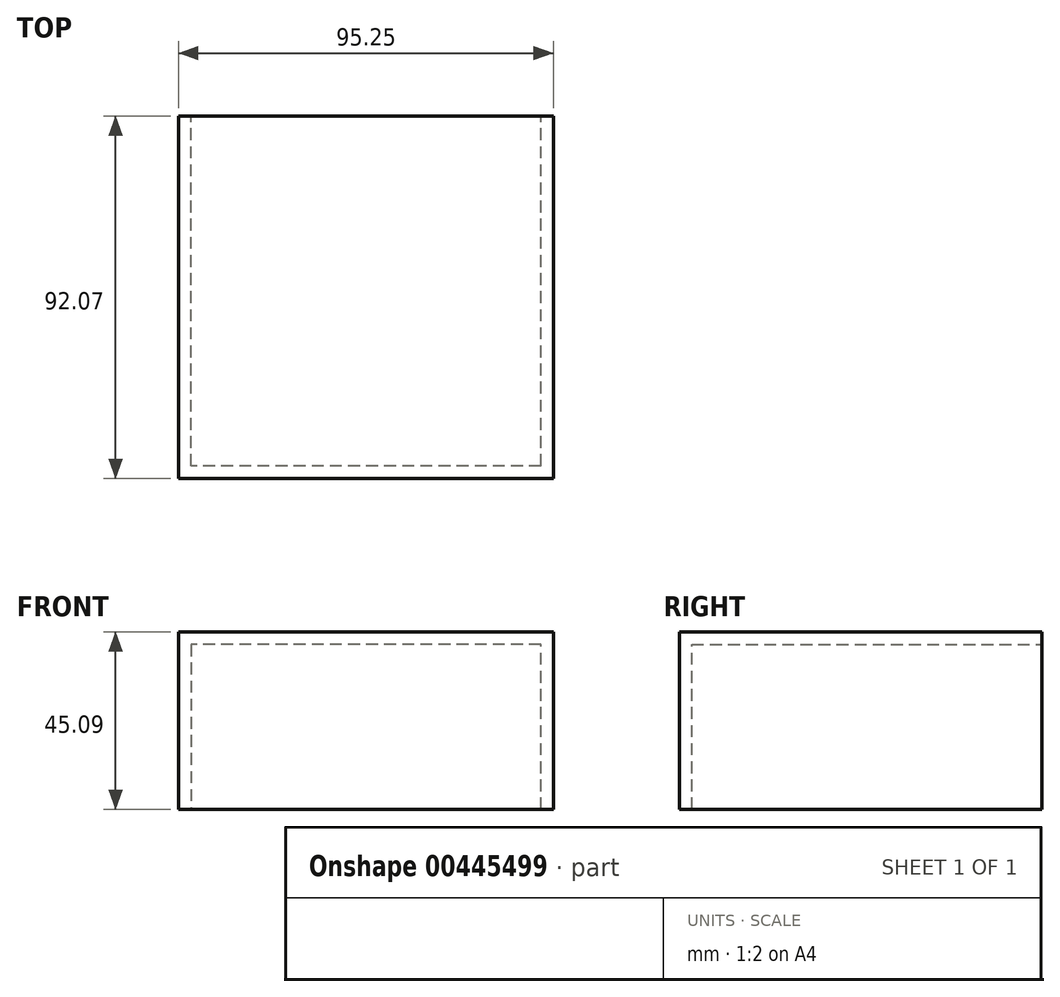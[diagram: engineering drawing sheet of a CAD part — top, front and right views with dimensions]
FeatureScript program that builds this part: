
annotation { "Feature Type Name" : "Feature", "Feature Type Description" : "" }
export const myFeature = defineFeature(function(context is Context, id is Id, definition is map)
    precondition{}
    {
        {
            var Q0;
            Q0=qCreatedBy(makeId("Front.planeOp"),FACE);
            var sketch = newSketch(context, id + "F0", { "sketchPlane" : qUnion([Q0])});
            skLineSegment(sketch, "E0", {"start": v(-34.9, -17.26) * mm, "end": v(-34.9, 24.65) * mm});
            skLineSegment(sketch, "E1", {"start": v(-34.9, 24.65) * mm, "end": v(54, 24.65) * mm});
            skLineSegment(sketch, "E2", {"start": v(54, 24.65) * mm, "end": v(54, -17.26) * mm});
            skLineSegment(sketch, "E3", {"start": v(-34.9, -17.26) * mm, "end": v(-38.07, -17.26) * mm});
            skLineSegment(sketch, "E4", {"start": v(-38.07, -17.26) * mm, "end": v(-38.07, 27.83) * mm});
            skLineSegment(sketch, "E5", {"start": v(-38.07, 27.83) * mm, "end": v(57.18, 27.83) * mm});
            skLineSegment(sketch, "E6", {"start": v(57.18, 27.83) * mm, "end": v(57.18, -17.26) * mm});
            skLineSegment(sketch, "E7", {"start": v(57.18, -17.26) * mm, "end": v(54, -17.26) * mm});
            skLineSegment(sketch, "E8.top", {"start": v(-38.07, -17.26) * mm, "end": v(57.18, -17.26) * mm});
            skLineSegment(sketch, "E8.left", {"start": v(-38.07, 27.83) * mm, "end": v(-38.07, -17.26) * mm});
            skArc(sketch, "E9", {"start": v(-5.18, 9.67) * mm, "mid": v(-18.9, 21.6) * mm, "end": v(-32.6, 9.67) * mm});
            skLineSegment(sketch, "E10", {"start": v(-32.6, 9.67) * mm, "end": v(-32.6, -17.26) * mm});
            skLineSegment(sketch, "E11", {"start": v(-5.18, 9.67) * mm, "end": v(-5.18, -17.26) * mm});
            skSolve(sketch);
        }
        {
            var Q0;
            {var subQ1=sQuery(id+"F0.wireOp",EDGE,"E0");Q0=makeQuery(id+"F0.imprint","IMPRINT",FACE,{"disambiguationData":[TD([[makeQuery(id+"F0.imprint","IMPRINT",EDGE,{"derivedFrom":subQ1}),1.0]])]});}
            extrude(context, id + "F1", {"entities" : qUnion([Q0]), "depth" : 114.3 * mm});
        }
        {
            var Q0;
            Q0=qCreatedBy(makeId("Front.planeOp"),FACE);
            var sketch = newSketch(context, id + "F2", { "sketchPlane" : qUnion([Q0])});
            skLineSegment(sketch, "E12.bottom", {"start": v(-38.05, 27.67) * mm, "end": v(57.2, 27.67) * mm});
            skLineSegment(sketch, "E12.top", {"start": v(-38.05, -17.41) * mm, "end": v(57.2, -17.41) * mm});
            skLineSegment(sketch, "E12.left", {"start": v(-38.05, 27.67) * mm, "end": v(-38.05, -17.41) * mm});
            skLineSegment(sketch, "E12.right", {"start": v(57.2, 27.67) * mm, "end": v(57.2, -17.41) * mm});
            skSolve(sketch);
        }
        {
            var Q0;
            Q0=makeQuery(id+"F1.opExtrude","CAP_FACE",FACE,{"disambiguationData":[OSD([sQuery(id+"F0.wireOp",EDGE,"E0"),sQuery(id+"F0.wireOp",EDGE,"E1"),sQuery(id+"F0.wireOp",EDGE,"E2"),sQuery(id+"F0.wireOp",EDGE,"E5"),sQuery(id+"F0.wireOp",EDGE,"E8.top"),sQuery(id+"F0.wireOp",EDGE,"E8.left"),sQuery(id+"F0.wireOp",EDGE,"E6")])],"isStart":false});
            var sketch = newSketch(context, id + "F3", { "sketchPlane" : qUnion([Q0])});
            skLineSegment(sketch, "E13.bottom", {"start": v(-38.07, 27.83) * mm, "end": v(57.18, 27.83) * mm});
            skLineSegment(sketch, "E13.top", {"start": v(-38.07, -17.26) * mm, "end": v(57.18, -17.26) * mm});
            skLineSegment(sketch, "E13.left", {"start": v(-38.07, 27.83) * mm, "end": v(-38.07, -17.26) * mm});
            skLineSegment(sketch, "E13.right", {"start": v(57.18, 27.83) * mm, "end": v(57.18, -17.26) * mm});
            skSolve(sketch);
        }
        {
            var Q0;
            Q0 = qSketchRegion(id + "F3", true);
            var Q1;
            Q1 = qSketchRegion(id + "F0", true);
            extrude(context, id + "F4", {"entities" : qUnion([Q0, Q1]), "operationType" : NewBodyOperationType.ADD, "depth" : 3.17 * mm});
        }
        {
            var Q0;
            Q0=makeQuery(id+"F2.imprint","IMPRINT",FACE,{"disambiguationData":[TD([[makeQuery(id+"F2.imprint","IMPRINT",EDGE,{"derivedFrom":sQuery(id+"F2.wireOp",EDGE,"E12.bottom")}),-1.0]])]});
            var sketch = newSketch(context, id + "F5", { "sketchPlane" : qUnion([Q0])});
            skCircle(sketch, "E14", {"center": v(-21.16, 10.78) * mm, "radius": 13.72 * mm});
            skLineSegment(sketch, "E15.bottom", {"start": v(-7.44, 10.78) * mm, "end": v(-34.88, 10.78) * mm});
            skLineSegment(sketch, "E15.top", {"start": v(-7.44, -18.14) * mm, "end": v(-34.88, -18.14) * mm});
            skLineSegment(sketch, "E15.left", {"start": v(-7.44, 10.78) * mm, "end": v(-7.44, -18.14) * mm});
            skLineSegment(sketch, "E15.right", {"start": v(-34.88, 10.78) * mm, "end": v(-34.88, -18.14) * mm});
            skSolve(sketch);
        }
        {
            var Q0;
            Q0=sQuery(id+"F5.wireOp",VERTEX,"E14.center");
            var Q1;
            Q1=makeQuery(id+"F1.opExtrude","SWEPT_BODY",BODY,{"disambiguationData":[OSD([sQuery(id+"F0.wireOp",EDGE,"E0"),sQuery(id+"F0.wireOp",EDGE,"E1"),sQuery(id+"F0.wireOp",EDGE,"E2"),sQuery(id+"F0.wireOp",EDGE,"E5"),sQuery(id+"F0.wireOp",EDGE,"E8.top"),sQuery(id+"F0.wireOp",EDGE,"E8.left"),sQuery(id+"F0.wireOp",EDGE,"E6")])]});
            hole(context, id + "F6", {"style" : HoleStyle.SIMPLE, "endStyle" : HoleEndStyle.BLIND, "oppositeDirection" : true, "holeDiameter" : 27.43 * mm, "holeDepth" : 3.17 * mm, "tappedDepth" : 12.7 * mm, "tapClearance" : 3, "startFromSketch" : true, "locations" : qUnion([Q0]), "scope" : qUnion([Q1])});
        }
        {
            var Q0;
            Q0 = qSketchRegion(id + "F5", true);
            extrude(context, id + "F7", {"entities" : qUnion([Q0]), "operationType" : NewBodyOperationType.REMOVE, "depth" : 3.17 * mm});
        }
        {
            var Q0;
            Q0=makeQuery(id+"F4.boolean.opBoolean","MERGE",FACE,{"derivedFrom":[makeQuery(id+"F1.opExtrude","SWEPT_FACE",FACE,{"disambiguationData":[OSD([sQuery(id+"F0.wireOp",EDGE,"E5")])]}),makeQuery(id+"F4.opExtrude","SWEPT_FACE",FACE,{"disambiguationData":[OSD([sQuery(id+"F3.wireOp",EDGE,"E13.bottom")])]})]});
            var sketch = newSketch(context, id + "F8", { "sketchPlane" : qUnion([Q0])});
            skLineSegment(sketch, "E16.bottom", {"start": v(57.18, 0) * mm, "end": v(-38.07, 0) * mm});
            skLineSegment(sketch, "E16.top", {"start": v(57.18, -25.4) * mm, "end": v(-38.07, -25.4) * mm});
            skLineSegment(sketch, "E16.left", {"start": v(57.18, 0) * mm, "end": v(57.18, -25.4) * mm});
            skLineSegment(sketch, "E16.right", {"start": v(-38.07, 0) * mm, "end": v(-38.07, -25.4) * mm});
            skSolve(sketch);
        }
        {
            var Q0;
            Q0 = qSketchRegion(id + "F8", true);
            extrude(context, id + "F9", {"entities" : qUnion([Q0]), "operationType" : NewBodyOperationType.REMOVE, "endBound" : BoundingType.THROUGH_ALL, "oppositeDirection" : true, "depth" : 25.4 * mm, "offsetDistance" : 25.4 * mm});
        }
    });
